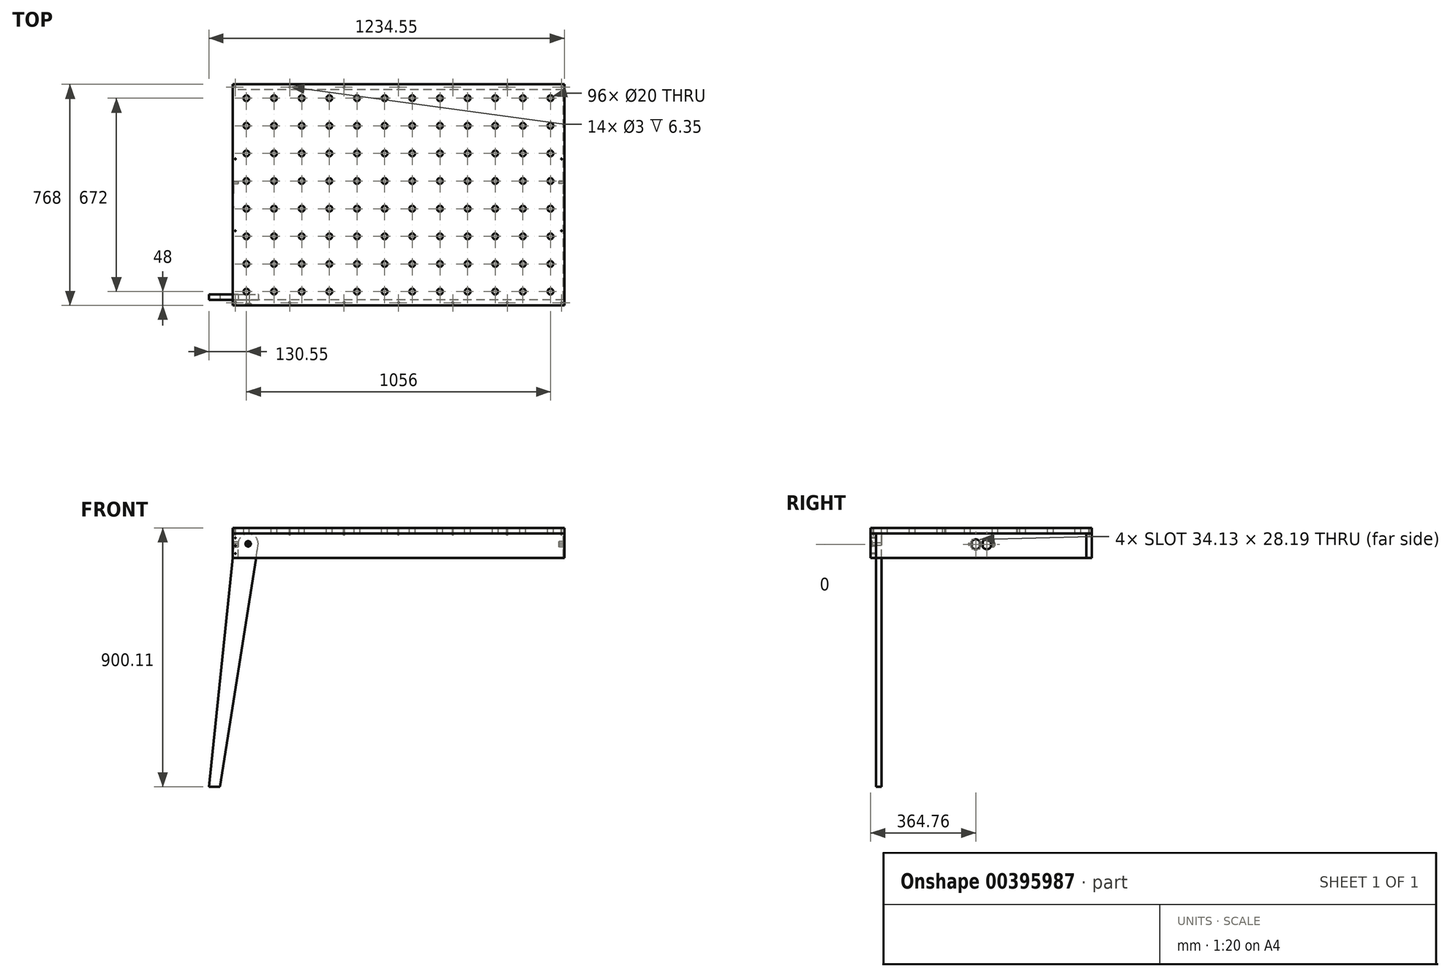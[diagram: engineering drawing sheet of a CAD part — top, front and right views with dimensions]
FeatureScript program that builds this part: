
annotation { "Feature Type Name" : "Feature", "Feature Type Description" : "" }
export const myFeature = defineFeature(function(context is Context, id is Id, definition is map)
    precondition{}
    {
        {
            var Q0;
            Q0=qCreatedBy(makeId("Top.planeOp"),FACE);
            var sketch = newSketch(context, id + "F0", { "sketchPlane" : qUnion([Q0])});
            skLineSegment(sketch, "E0.bottom", {"start": v(0, 0) * mm, "end": v(1152, 0) * mm});
            skLineSegment(sketch, "E0.top", {"start": v(0, 768) * mm, "end": v(1152, 768) * mm});
            skLineSegment(sketch, "E0.left", {"start": v(0, 0) * mm, "end": v(0, 768) * mm});
            skLineSegment(sketch, "E0.right", {"start": v(1152, 0) * mm, "end": v(1152, 768) * mm});
            skSolve(sketch);
        }
        {
            var Q0;
            Q0=makeQuery(id+"F0.imprint","IMPRINT",FACE,{"disambiguationData":[TD([[makeQuery(id+"F0.imprint","IMPRINT",EDGE,{"derivedFrom":sQuery(id+"F0.wireOp",EDGE,"E0.bottom")}),1.0]])]});
            extrude(context, id + "F1", {"entities" : qUnion([Q0]), "depth" : 19.05 * mm});
        }
        {
            var Q0;
            Q0=makeQuery(id+"F1.opExtrude","CAP_FACE",FACE,{"disambiguationData":[OSD([sQuery(id+"F0.wireOp",EDGE,"E0.bottom"),sQuery(id+"F0.wireOp",EDGE,"E0.top"),sQuery(id+"F0.wireOp",EDGE,"E0.left"),sQuery(id+"F0.wireOp",EDGE,"E0.right")])],"isStart":false});
            var sketch = newSketch(context, id + "F2", { "sketchPlane" : qUnion([Q0])});
            skLineSegment(sketch, "E1.0", {"start": v(1104, 720) * mm, "end": v(48, 720) * mm, "construction": true});
            skLineSegment(sketch, "E1.1", {"start": v(1104, 48) * mm, "end": v(1104, 720) * mm, "construction": true});
            skLineSegment(sketch, "E1.2", {"start": v(48, 48) * mm, "end": v(1104, 48) * mm, "construction": true});
            skLineSegment(sketch, "E1.3", {"start": v(48, 720) * mm, "end": v(48, 48) * mm, "construction": true});
            skCircle(sketch, "E2", {"center": v(48, 48) * mm, "radius": 10 * mm});
            skCircle(sketch, "E3.0.1.0", {"center": v(48, 144) * mm, "radius": 10 * mm});
            skCircle(sketch, "E3.0.2.0", {"center": v(48, 240) * mm, "radius": 10 * mm});
            skCircle(sketch, "E3.0.3.0", {"center": v(48, 336) * mm, "radius": 10 * mm});
            skCircle(sketch, "E3.0.4.0", {"center": v(48, 432) * mm, "radius": 10 * mm});
            skCircle(sketch, "E3.0.5.0", {"center": v(48, 528) * mm, "radius": 10 * mm});
            skCircle(sketch, "E3.0.6.0", {"center": v(48, 624) * mm, "radius": 10 * mm});
            skCircle(sketch, "E3.0.7.0", {"center": v(48, 720) * mm, "radius": 10 * mm});
            skCircle(sketch, "E3.1.0.0", {"center": v(144, 48) * mm, "radius": 10 * mm});
            skCircle(sketch, "E3.1.1.0", {"center": v(144, 144) * mm, "radius": 10 * mm});
            skCircle(sketch, "E3.1.2.0", {"center": v(144, 240) * mm, "radius": 10 * mm});
            skCircle(sketch, "E3.1.3.0", {"center": v(144, 336) * mm, "radius": 10 * mm});
            skCircle(sketch, "E3.1.4.0", {"center": v(144, 432) * mm, "radius": 10 * mm});
            skCircle(sketch, "E3.1.5.0", {"center": v(144, 528) * mm, "radius": 10 * mm});
            skCircle(sketch, "E3.1.6.0", {"center": v(144, 624) * mm, "radius": 10 * mm});
            skCircle(sketch, "E3.1.7.0", {"center": v(144, 720) * mm, "radius": 10 * mm});
            skCircle(sketch, "E3.2.0.0", {"center": v(240, 48) * mm, "radius": 10 * mm});
            skCircle(sketch, "E3.2.1.0", {"center": v(240, 144) * mm, "radius": 10 * mm});
            skCircle(sketch, "E3.2.2.0", {"center": v(240, 240) * mm, "radius": 10 * mm});
            skCircle(sketch, "E3.2.3.0", {"center": v(240, 336) * mm, "radius": 10 * mm});
            skCircle(sketch, "E3.2.4.0", {"center": v(240, 432) * mm, "radius": 10 * mm});
            skCircle(sketch, "E3.2.5.0", {"center": v(240, 528) * mm, "radius": 10 * mm});
            skCircle(sketch, "E3.2.6.0", {"center": v(240, 624) * mm, "radius": 10 * mm});
            skCircle(sketch, "E3.2.7.0", {"center": v(240, 720) * mm, "radius": 10 * mm});
            skCircle(sketch, "E3.3.0.0", {"center": v(336, 48) * mm, "radius": 10 * mm});
            skCircle(sketch, "E3.3.1.0", {"center": v(336, 144) * mm, "radius": 10 * mm});
            skCircle(sketch, "E3.3.2.0", {"center": v(336, 240) * mm, "radius": 10 * mm});
            skCircle(sketch, "E3.3.3.0", {"center": v(336, 336) * mm, "radius": 10 * mm});
            skCircle(sketch, "E3.3.4.0", {"center": v(336, 432) * mm, "radius": 10 * mm});
            skCircle(sketch, "E3.3.5.0", {"center": v(336, 528) * mm, "radius": 10 * mm});
            skCircle(sketch, "E3.3.6.0", {"center": v(336, 624) * mm, "radius": 10 * mm});
            skCircle(sketch, "E3.3.7.0", {"center": v(336, 720) * mm, "radius": 10 * mm});
            skCircle(sketch, "E3.4.0.0", {"center": v(432, 48) * mm, "radius": 10 * mm});
            skCircle(sketch, "E3.4.1.0", {"center": v(432, 144) * mm, "radius": 10 * mm});
            skCircle(sketch, "E3.4.2.0", {"center": v(432, 240) * mm, "radius": 10 * mm});
            skCircle(sketch, "E3.4.3.0", {"center": v(432, 336) * mm, "radius": 10 * mm});
            skCircle(sketch, "E3.4.4.0", {"center": v(432, 432) * mm, "radius": 10 * mm});
            skCircle(sketch, "E3.4.5.0", {"center": v(432, 528) * mm, "radius": 10 * mm});
            skCircle(sketch, "E3.4.6.0", {"center": v(432, 624) * mm, "radius": 10 * mm});
            skCircle(sketch, "E3.4.7.0", {"center": v(432, 720) * mm, "radius": 10 * mm});
            skCircle(sketch, "E3.5.0.0", {"center": v(528, 48) * mm, "radius": 10 * mm});
            skCircle(sketch, "E3.5.1.0", {"center": v(528, 144) * mm, "radius": 10 * mm});
            skCircle(sketch, "E3.5.2.0", {"center": v(528, 240) * mm, "radius": 10 * mm});
            skCircle(sketch, "E3.5.3.0", {"center": v(528, 336) * mm, "radius": 10 * mm});
            skCircle(sketch, "E3.5.4.0", {"center": v(528, 432) * mm, "radius": 10 * mm});
            skCircle(sketch, "E3.5.5.0", {"center": v(528, 528) * mm, "radius": 10 * mm});
            skCircle(sketch, "E3.5.6.0", {"center": v(528, 624) * mm, "radius": 10 * mm});
            skCircle(sketch, "E3.5.7.0", {"center": v(528, 720) * mm, "radius": 10 * mm});
            skCircle(sketch, "E3.6.0.0", {"center": v(624, 48) * mm, "radius": 10 * mm});
            skCircle(sketch, "E3.6.1.0", {"center": v(624, 144) * mm, "radius": 10 * mm});
            skCircle(sketch, "E3.6.2.0", {"center": v(624, 240) * mm, "radius": 10 * mm});
            skCircle(sketch, "E3.6.3.0", {"center": v(624, 336) * mm, "radius": 10 * mm});
            skCircle(sketch, "E3.6.4.0", {"center": v(624, 432) * mm, "radius": 10 * mm});
            skCircle(sketch, "E3.6.5.0", {"center": v(624, 528) * mm, "radius": 10 * mm});
            skCircle(sketch, "E3.6.6.0", {"center": v(624, 624) * mm, "radius": 10 * mm});
            skCircle(sketch, "E3.6.7.0", {"center": v(624, 720) * mm, "radius": 10 * mm});
            skCircle(sketch, "E3.7.0.0", {"center": v(720, 48) * mm, "radius": 10 * mm});
            skCircle(sketch, "E3.7.1.0", {"center": v(720, 144) * mm, "radius": 10 * mm});
            skCircle(sketch, "E3.7.2.0", {"center": v(720, 240) * mm, "radius": 10 * mm});
            skCircle(sketch, "E3.7.3.0", {"center": v(720, 336) * mm, "radius": 10 * mm});
            skCircle(sketch, "E3.7.4.0", {"center": v(720, 432) * mm, "radius": 10 * mm});
            skCircle(sketch, "E3.7.5.0", {"center": v(720, 528) * mm, "radius": 10 * mm});
            skCircle(sketch, "E3.7.6.0", {"center": v(720, 624) * mm, "radius": 10 * mm});
            skCircle(sketch, "E3.7.7.0", {"center": v(720, 720) * mm, "radius": 10 * mm});
            skCircle(sketch, "E3.8.0.0", {"center": v(816, 48) * mm, "radius": 10 * mm});
            skCircle(sketch, "E3.8.1.0", {"center": v(816, 144) * mm, "radius": 10 * mm});
            skCircle(sketch, "E3.8.2.0", {"center": v(816, 240) * mm, "radius": 10 * mm});
            skCircle(sketch, "E3.8.3.0", {"center": v(816, 336) * mm, "radius": 10 * mm});
            skCircle(sketch, "E3.8.4.0", {"center": v(816, 432) * mm, "radius": 10 * mm});
            skCircle(sketch, "E3.8.5.0", {"center": v(816, 528) * mm, "radius": 10 * mm});
            skCircle(sketch, "E3.8.6.0", {"center": v(816, 624) * mm, "radius": 10 * mm});
            skCircle(sketch, "E3.8.7.0", {"center": v(816, 720) * mm, "radius": 10 * mm});
            skCircle(sketch, "E3.9.0.0", {"center": v(912, 48) * mm, "radius": 10 * mm});
            skCircle(sketch, "E3.9.1.0", {"center": v(912, 144) * mm, "radius": 10 * mm});
            skCircle(sketch, "E3.9.2.0", {"center": v(912, 240) * mm, "radius": 10 * mm});
            skCircle(sketch, "E3.9.3.0", {"center": v(912, 336) * mm, "radius": 10 * mm});
            skCircle(sketch, "E3.9.4.0", {"center": v(912, 432) * mm, "radius": 10 * mm});
            skCircle(sketch, "E3.9.5.0", {"center": v(912, 528) * mm, "radius": 10 * mm});
            skCircle(sketch, "E3.9.6.0", {"center": v(912, 624) * mm, "radius": 10 * mm});
            skCircle(sketch, "E3.9.7.0", {"center": v(912, 720) * mm, "radius": 10 * mm});
            skCircle(sketch, "E3.10.0.0", {"center": v(1008, 48) * mm, "radius": 10 * mm});
            skCircle(sketch, "E3.10.1.0", {"center": v(1008, 144) * mm, "radius": 10 * mm});
            skCircle(sketch, "E3.10.2.0", {"center": v(1008, 240) * mm, "radius": 10 * mm});
            skCircle(sketch, "E3.10.3.0", {"center": v(1008, 336) * mm, "radius": 10 * mm});
            skCircle(sketch, "E3.10.4.0", {"center": v(1008, 432) * mm, "radius": 10 * mm});
            skCircle(sketch, "E3.10.5.0", {"center": v(1008, 528) * mm, "radius": 10 * mm});
            skCircle(sketch, "E3.10.6.0", {"center": v(1008, 624) * mm, "radius": 10 * mm});
            skCircle(sketch, "E3.10.7.0", {"center": v(1008, 720) * mm, "radius": 10 * mm});
            skCircle(sketch, "E3.11.0.0", {"center": v(1104, 48) * mm, "radius": 10 * mm});
            skCircle(sketch, "E3.11.1.0", {"center": v(1104, 144) * mm, "radius": 10 * mm});
            skCircle(sketch, "E3.11.2.0", {"center": v(1104, 240) * mm, "radius": 10 * mm});
            skCircle(sketch, "E3.11.3.0", {"center": v(1104, 336) * mm, "radius": 10 * mm});
            skCircle(sketch, "E3.11.4.0", {"center": v(1104, 432) * mm, "radius": 10 * mm});
            skCircle(sketch, "E3.11.5.0", {"center": v(1104, 528) * mm, "radius": 10 * mm});
            skCircle(sketch, "E3.11.6.0", {"center": v(1104, 624) * mm, "radius": 10 * mm});
            skCircle(sketch, "E3.11.7.0", {"center": v(1104, 720) * mm, "radius": 10 * mm});
            skLineSegment(sketch, "E3.direction1", {"start": v(48, 48) * mm, "end": v(144, 48) * mm, "construction": true});
            skLineSegment(sketch, "E3.direction2", {"start": v(48, 48) * mm, "end": v(48, 144) * mm, "construction": true});
            skSolve(sketch);
        }
        {
            var Q0;
            Q0=qSketchRegion(id+"F2",true);
            extrude(context, id + "F3", {"entities" : qUnion([Q0]), "operationType" : NewBodyOperationType.REMOVE, "endBound" : BoundingType.THROUGH_ALL, "oppositeDirection" : true, "depth" : 25.4 * mm});
        }
        {
            var Q0;
            Q0=qCreatedBy(makeId("Right.planeOp"),FACE);
            var sketch = newSketch(context, id + "F4", { "sketchPlane" : qUnion([Q0])});
            skLineSegment(sketch, "E4.bottom", {"start": v(0, 0) * mm, "end": v(19.05, 0) * mm});
            skLineSegment(sketch, "E4.top", {"start": v(0, -85.95) * mm, "end": v(19.05, -85.95) * mm});
            skLineSegment(sketch, "E4.left", {"start": v(0, 0) * mm, "end": v(0, -85.95) * mm});
            skLineSegment(sketch, "E4.right", {"start": v(19.05, 0) * mm, "end": v(19.05, -85.95) * mm});
            skSolve(sketch);
        }
        {
            var Q0;
            Q0=qSketchRegion(id+"F4",true);
            var Q1;
            Q1=makeQuery(id+"F1.opExtrude","SWEPT_FACE",FACE,{"disambiguationData":[OSD([sQuery(id+"F0.wireOp",EDGE,"E0.right")])]});
            extrude(context, id + "F5", {"entities" : qUnion([Q0]), "endBound" : BoundingType.UP_TO_SURFACE, "endBoundEntityFace" : qUnion([Q1]), "depth" : 25.4 * mm});
        }
        {
            var Q0;
            Q0=makeQuery(id+"F5.opExtrude","SWEPT_FACE",FACE,{"disambiguationData":[OSD([sQuery(id+"F4.wireOp",EDGE,"E4.right")])]});
            var sketch = newSketch(context, id + "F6", { "sketchPlane" : qUnion([Q0])});
            skLineSegment(sketch, "E5.bottom", {"start": v(0, 0) * mm, "end": v(-19.05, 0) * mm});
            skLineSegment(sketch, "E5.top", {"start": v(0, -85.95) * mm, "end": v(-19.05, -85.95) * mm});
            skLineSegment(sketch, "E5.left", {"start": v(0, 0) * mm, "end": v(0, -85.95) * mm});
            skLineSegment(sketch, "E5.right", {"start": v(-19.05, 0) * mm, "end": v(-19.05, -85.95) * mm});
            skSolve(sketch);
        }
        {
            var Q0;
            Q0=makeQuery(id+"F1.opExtrude","CAP_FACE",FACE,{"disambiguationData":[OSD([sQuery(id+"F0.wireOp",EDGE,"E0.bottom"),sQuery(id+"F0.wireOp",EDGE,"E0.top"),sQuery(id+"F0.wireOp",EDGE,"E0.left"),sQuery(id+"F0.wireOp",EDGE,"E0.right")])],"isStart":false});
            var sketch = newSketch(context, id + "F7", { "sketchPlane" : qUnion([Q0])});
            skCircle(sketch, "E6", {"center": v(9.52, 9.53) * mm, "radius": 1.5 * mm});
            skCircle(sketch, "E7", {"center": v(198.35, 9.53) * mm, "radius": 1.5 * mm});
            skCircle(sketch, "E8", {"center": v(387.18, 9.53) * mm, "radius": 1.5 * mm});
            skCircle(sketch, "E9", {"center": v(576, 9.53) * mm, "radius": 1.5 * mm});
            skCircle(sketch, "E10", {"center": v(764.83, 9.53) * mm, "radius": 1.5 * mm});
            skCircle(sketch, "E11", {"center": v(953.65, 9.53) * mm, "radius": 1.5 * mm});
            skCircle(sketch, "E12", {"center": v(1142.48, 9.53) * mm, "radius": 1.5 * mm});
            skLineSegment(sketch, "E13", {"start": v(9.53, 9.53) * mm, "end": v(198.35, 9.53) * mm, "construction": true});
            skLineSegment(sketch, "E14", {"start": v(387.18, 9.53) * mm, "end": v(198.35, 9.53) * mm, "construction": true});
            skLineSegment(sketch, "E15", {"start": v(387.18, 9.53) * mm, "end": v(576, 9.53) * mm, "construction": true});
            skLineSegment(sketch, "E16", {"start": v(576, 9.53) * mm, "end": v(764.83, 9.53) * mm, "construction": true});
            skLineSegment(sketch, "E17", {"start": v(764.83, 9.53) * mm, "end": v(953.65, 9.53) * mm, "construction": true});
            skLineSegment(sketch, "E18", {"start": v(953.65, 9.53) * mm, "end": v(1142.48, 9.53) * mm, "construction": true});
            skLineSegment(sketch, "E19", {"start": v(1142.48, 9.53) * mm, "end": v(1152, 9.53) * mm, "construction": true});
            skLineSegment(sketch, "E20", {"start": v(1142.48, 9.53) * mm, "end": v(1142.48, 0) * mm, "construction": true});
            skLineSegment(sketch, "E21", {"start": v(9.52, 9.53) * mm, "end": v(0, 9.53) * mm, "construction": true});
            skCircle(sketch, "E22", {"center": v(9.52, 259.18) * mm, "radius": 1.5 * mm});
            skCircle(sketch, "E23", {"center": v(9.52, 508.83) * mm, "radius": 1.5 * mm});
            skCircle(sketch, "E24", {"center": v(9.52, 758.48) * mm, "radius": 1.5 * mm});
            skLineSegment(sketch, "E25", {"start": v(9.52, 758.48) * mm, "end": v(9.52, 768) * mm, "construction": true});
            skLineSegment(sketch, "E26", {"start": v(9.52, 9.53) * mm, "end": v(9.53, 0) * mm, "construction": true});
            skLineSegment(sketch, "E27", {"start": v(9.52, 9.53) * mm, "end": v(9.52, 259.18) * mm, "construction": true});
            skLineSegment(sketch, "E28", {"start": v(9.52, 259.18) * mm, "end": v(9.52, 508.83) * mm, "construction": true});
            skLineSegment(sketch, "E29", {"start": v(9.52, 508.83) * mm, "end": v(9.52, 758.48) * mm, "construction": true});
            skLineSegment(sketch, "E30", {"start": v(0, 384) * mm, "end": v(1152, 384) * mm, "construction": true});
            skLineSegment(sketch, "E31", {"start": v(576, 768) * mm, "end": v(576, 0) * mm, "construction": true});
            skCircle(sketch, "E32.MirrorC", {"center": v(1142.48, 758.48) * mm, "radius": 1.5 * mm});
            skCircle(sketch, "E33.MirrorC", {"center": v(1142.48, 259.18) * mm, "radius": 1.5 * mm});
            skCircle(sketch, "E34.MirrorC", {"center": v(1142.48, 508.83) * mm, "radius": 1.5 * mm});
            skCircle(sketch, "E35.MirrorC", {"center": v(198.35, 758.48) * mm, "radius": 1.5 * mm});
            skCircle(sketch, "E36.MirrorC", {"center": v(387.18, 758.48) * mm, "radius": 1.5 * mm});
            skCircle(sketch, "E37.MirrorC", {"center": v(576, 758.48) * mm, "radius": 1.5 * mm});
            skCircle(sketch, "E38.MirrorC", {"center": v(764.83, 758.47) * mm, "radius": 1.5 * mm});
            skCircle(sketch, "E39.MirrorC", {"center": v(953.65, 758.47) * mm, "radius": 1.5 * mm});
            skSolve(sketch);
        }
        {
            var Q0;
            Q0=sQuery(id+"F7.wireOp",EDGE,"E30");
            cPlane(context, id + "F8", {"entities" : qUnion([Q0]), "cplaneType" : CPlaneType.LINE_ANGLE, "offset" : 25.4 * mm, "angle" : 0 * degree, "width" : 152.4 * mm, "height" : 152.4 * mm});
        }
        {
            var Q0;
            Q0=makeQuery(id+"F5.opExtrude","SWEPT_BODY",BODY,{"disambiguationData":[OSD([sQuery(id+"F4.wireOp",EDGE,"E4.bottom"),sQuery(id+"F4.wireOp",EDGE,"E4.top"),sQuery(id+"F4.wireOp",EDGE,"E4.left"),sQuery(id+"F4.wireOp",EDGE,"E4.right")])]});
            var Q1;
            Q1=qCreatedBy(id+"F8.planeOp",FACE);
            mirror(context, id + "F9", {"entities" : qUnion([Q0]), "mirrorPlane" : qUnion([Q1])});
        }
        {
            var Q0;
            Q0=makeQuery(id+"F6.imprint","IMPRINT",FACE,{"disambiguationData":[TD([[makeQuery(id+"F6.imprint","IMPRINT",EDGE,{"derivedFrom":sQuery(id+"F6.wireOp",EDGE,"E5.bottom")}),-1.0]])]});
            var Q1;
            Q1=makeQuery(id+"F9.opPattern","COPY",FACE,{"derivedFrom":makeQuery(id+"F5.opExtrude","SWEPT_FACE",FACE,{"disambiguationData":[OSD([sQuery(id+"F4.wireOp",EDGE,"E4.right")])]}),"instanceName":"1"});
            extrude(context, id + "F10", {"entities" : qUnion([Q0]), "endBound" : BoundingType.UP_TO_SURFACE, "endBoundEntityFace" : qUnion([Q1]), "depth" : 25.4 * mm});
        }
        {
            var Q0;
            Q0=qSketchRegion(id+"F7",true);
            extrude(context, id + "F11", {"entities" : qUnion([Q0]), "operationType" : NewBodyOperationType.REMOVE, "oppositeDirection" : true, "depth" : 25.4 * mm});
        }
        {
            var Q0;
            Q0=makeQuery(id+"F5.opExtrude","SWEPT_FACE",FACE,{"disambiguationData":[OSD([sQuery(id+"F4.wireOp",EDGE,"E4.right")])]});
            var sketch = newSketch(context, id + "F12", { "sketchPlane" : qUnion([Q0])});
            skLineSegment(sketch, "E40", {"start": v(-19.05, -36.51) * mm, "end": v(-19.05, -881.06) * mm, "construction": true});
            skLineSegment(sketch, "E41", {"start": v(44.45, -881.06) * mm, "end": v(-88.47, -41.98) * mm});
            skArc(sketch, "E42", {"start": v(-19.05, -36.51) * mm, "mid": v(-56.72, -1.7) * mm, "end": v(-88.47, -41.98) * mm});
            skLineSegment(sketch, "E43", {"start": v(-19.05, -85.95) * mm, "end": v(0, -85.95) * mm});
            skLineSegment(sketch, "E44", {"start": v(0, -85.95) * mm, "end": v(82.55, -881.06) * mm});
            skLineSegment(sketch, "E45", {"start": v(82.55, -881.06) * mm, "end": v(44.45, -881.06) * mm});
            skLineSegment(sketch, "E46", {"start": v(-19.05, -881.06) * mm, "end": v(-19.05, 19.05) * mm, "construction": true});
            skLineSegment(sketch, "E47", {"start": v(-19.05, -85.95) * mm, "end": v(-19.05, -36.51) * mm});
            skSolve(sketch);
        }
        {
            var Q0;
            Q0=qSketchRegion(id+"F12",true);
            extrude(context, id + "F13", {"entities" : qUnion([Q0]), "depth" : 19.05 * mm});
        }
        {
            var Q0;
            Q0=makeQuery(id+"F13.opExtrude","CAP_FACE",FACE,{"disambiguationData":[OSD([sQuery(id+"F12.wireOp",EDGE,"E41"),sQuery(id+"F12.wireOp",EDGE,"E42"),sQuery(id+"F12.wireOp",EDGE,"E43"),sQuery(id+"F12.wireOp",EDGE,"E44"),sQuery(id+"F12.wireOp",EDGE,"E45"),sQuery(id+"F12.wireOp",EDGE,"E47")])],"isStart":false});
            var sketch = newSketch(context, id + "F14", { "sketchPlane" : qUnion([Q0])});
            skCircle(sketch, "E48", {"center": v(-53.97, -36.51) * mm, "radius": 4.76 * mm});
            skSolve(sketch);
        }
        {
            var Q0;
            Q0=qSketchRegion(id+"F14",true);
            extrude(context, id + "F15", {"entities" : qUnion([Q0]), "operationType" : NewBodyOperationType.REMOVE, "endBound" : BoundingType.THROUGH_ALL, "oppositeDirection" : true, "depth" : 25.4 * mm});
        }
        {
            var Q0;
            Q0=makeQuery(id+"F5.opExtrude","SWEPT_FACE",FACE,{"disambiguationData":[OSD([sQuery(id+"F4.wireOp",EDGE,"E4.left")])]});
            var sketch = newSketch(context, id + "F16", { "sketchPlane" : qUnion([Q0])});
            skCircle(sketch, "E49", {"center": v(53.97, -36.51) * mm, "radius": 9.53 * mm});
            skSolve(sketch);
        }
        {
            var Q0;
            Q0=qSketchRegion(id+"F16",true);
            extrude(context, id + "F17", {"entities" : qUnion([Q0]), "operationType" : NewBodyOperationType.REMOVE, "oppositeDirection" : true, "depth" : 6.35 * mm});
        }
        {
            var Q0;
            Q0=makeQuery(id+"F5.opExtrude","SWEPT_FACE",FACE,{"disambiguationData":[OSD([sQuery(id+"F4.wireOp",EDGE,"E4.left")])]});
            var sketch = newSketch(context, id + "F18", { "sketchPlane" : qUnion([Q0])});
            skCircle(sketch, "E50", {"center": v(9.52, -15.88) * mm, "radius": 1.5 * mm});
            skCircle(sketch, "E51", {"center": v(9.53, -42.98) * mm, "radius": 1.5 * mm});
            skCircle(sketch, "E52", {"center": v(9.53, -70.08) * mm, "radius": 1.5 * mm});
            skLineSegment(sketch, "E53", {"start": v(9.52, 0) * mm, "end": v(9.52, -15.88) * mm, "construction": true});
            skLineSegment(sketch, "E54", {"start": v(9.53, -85.95) * mm, "end": v(9.53, -70.08) * mm, "construction": true});
            skLineSegment(sketch, "E55", {"start": v(9.52, -15.88) * mm, "end": v(9.53, -70.08) * mm, "construction": true});
            skSolve(sketch);
        }
        {
            var Q0;
            Q0=qSketchRegion(id+"F18",true);
            extrude(context, id + "F19", {"entities" : qUnion([Q0]), "operationType" : NewBodyOperationType.REMOVE, "oppositeDirection" : true, "depth" : 41.27 * mm});
        }
        {
            var Q0;
            Q0=makeQuery(id+"F10.opExtrude","SWEPT_FACE",FACE,{"disambiguationData":[OSD([sQuery(id+"F6.wireOp",EDGE,"E5.right")])]});
            var sketch = newSketch(context, id + "F20", { "sketchPlane" : qUnion([Q0])});
            skLineSegment(sketch, "E56.bottom", {"start": v(422.9, -12.7) * mm, "end": v(345.1, -12.7) * mm});
            skLineSegment(sketch, "E56.top", {"start": v(422.9, -63.5) * mm, "end": v(345.1, -63.5) * mm});
            skLineSegment(sketch, "E56.left", {"start": v(422.9, -12.7) * mm, "end": v(422.9, -63.5) * mm});
            skLineSegment(sketch, "E56.right", {"start": v(345.1, -12.7) * mm, "end": v(345.1, -63.5) * mm});
            skPoint(sketch, "E56.middle", {"position": v(384, -38.1) * mm});
            skPoint(sketch, "E56.middle.positionSnap0", {"position": v(384, 0) * mm});
            skPoint(sketch, "E56.centerSnap0", {"position": v(384, 0) * mm});
            skSolve(sketch);
        }
        {
            var Q0;
            Q0=makeQuery(id+"F20.imprint","IMPRINT",FACE,{"disambiguationData":[TD([[makeQuery(id+"F20.imprint","IMPRINT",EDGE,{"derivedFrom":sQuery(id+"F20.wireOp",EDGE,"E56.bottom")}),1.0]])]});
            extrude(context, id + "F21", {"entities" : qUnion([Q0]), "operationType" : NewBodyOperationType.REMOVE, "oppositeDirection" : true, "depth" : 15.88 * mm});
        }
        {
            var Q0;
            Q0=makeQuery(id+"F21.boolean.opBoolean","COPY",FACE,{"derivedFrom":makeQuery(id+"F21.opExtrude","CAP_FACE",FACE,{"disambiguationData":[OSD([sQuery(id+"F20.wireOp",EDGE,"E56.bottom"),sQuery(id+"F20.wireOp",EDGE,"E56.top"),sQuery(id+"F20.wireOp",EDGE,"E56.left"),sQuery(id+"F20.wireOp",EDGE,"E56.right")])],"isStart":false})});
            var sketch = newSketch(context, id + "F22", { "sketchPlane" : qUnion([Q0])});
            skArc(sketch, "E57", {"start": v(389.14, -47.72) * mm, "mid": v(403.24, -55.17) * mm, "end": v(417.34, -47.72) * mm});
            skArc(sketch, "E58", {"start": v(350.66, -47.72) * mm, "mid": v(364.76, -55.17) * mm, "end": v(378.86, -47.72) * mm});
            skLineSegment(sketch, "E59", {"start": v(350.66, -47.72) * mm, "end": v(350.66, -28.48) * mm});
            skLineSegment(sketch, "E60", {"start": v(378.86, -28.48) * mm, "end": v(378.86, -47.72) * mm});
            skLineSegment(sketch, "E61", {"start": v(389.14, -28.48) * mm, "end": v(389.14, -47.72) * mm});
            skLineSegment(sketch, "E62", {"start": v(417.34, -28.48) * mm, "end": v(417.34, -47.72) * mm});
            skLineSegment(sketch, "E63", {"start": v(350.66, -28.48) * mm, "end": v(378.86, -28.48) * mm, "construction": true});
            skLineSegment(sketch, "E64", {"start": v(389.14, -28.48) * mm, "end": v(417.34, -28.48) * mm, "construction": true});
            skLineSegment(sketch, "E65", {"start": v(345.1, -38.1) * mm, "end": v(422.9, -38.1) * mm, "construction": true});
            skLineSegment(sketch, "E66", {"start": v(364.76, -38.1) * mm, "end": v(403.24, -38.1) * mm, "construction": true});
            skLineSegment(sketch, "E67", {"start": v(384, -38.1) * mm, "end": v(384, -43.41) * mm, "construction": true});
            skArc(sketch, "E68.trimOffspring", {"start": v(378.86, -28.48) * mm, "mid": v(364.76, -21.03) * mm, "end": v(350.66, -28.48) * mm});
            skLineSegment(sketch, "E69.trimOffspring", {"start": v(381.83, -38.1) * mm, "end": v(381.83, -38.1) * mm});
            skLineSegment(sketch, "E70.trimOffspring", {"start": v(386.17, -38.1) * mm, "end": v(386.17, -38.1) * mm});
            skArc(sketch, "E71.trimOffspring", {"start": v(417.34, -28.48) * mm, "mid": v(403.24, -21.03) * mm, "end": v(389.14, -28.48) * mm});
            skSolve(sketch);
        }
        {
            var Q0;
            Q0=qSketchRegion(id+"F22",true);
            extrude(context, id + "F23", {"entities" : qUnion([Q0]), "operationType" : NewBodyOperationType.REMOVE, "endBound" : BoundingType.THROUGH_ALL, "oppositeDirection" : true, "depth" : 25.4 * mm});
        }
        {
            var Q0;
            Q0=makeQuery(id+"F10.opExtrude","SWEPT_FACE",FACE,{"disambiguationData":[OSD([sQuery(id+"F6.wireOp",EDGE,"E5.right")])]});
            var sketch = newSketch(context, id + "F24", { "sketchPlane" : qUnion([Q0])});
            skArc(sketch, "E72", {"start": v(345.1, -28.57) * mm, "mid": v(335.58, -38.1) * mm, "end": v(345.1, -47.62) * mm});
            skArc(sketch, "E73.MirrorCS", {"start": v(345.1, 3.18) * mm, "mid": v(335.58, 12.7) * mm, "end": v(345.1, 22.23) * mm});
            skLineSegment(sketch, "E74", {"start": v(384, -12.7) * mm, "end": v(384, -63.5) * mm, "construction": true});
            skArc(sketch, "E75.MirrorCS", {"start": v(422.9, -28.57) * mm, "mid": v(432.42, -38.1) * mm, "end": v(422.9, -47.62) * mm});
            skSolve(sketch);
        }
        {
            var Q0;
            {var subQ0=sQuery(id+"F24.wireOp",EDGE,"E72");Q0=makeQuery(id+"F24.imprint","IMPRINT",FACE,{"disambiguationData":[TD([[makeQuery(id+"F24.imprint","IMPRINT",EDGE,{"derivedFrom":subQ0}),1.0]])]});}
            var Q1;
            {var subQ0=sQuery(id+"F24.wireOp",EDGE,"E75.MirrorCS");Q1=makeQuery(id+"F24.imprint","IMPRINT",FACE,{"disambiguationData":[TD([[makeQuery(id+"F24.imprint","IMPRINT",EDGE,{"derivedFrom":subQ0}),-1.0]])]});}
            var Q2;
            Q2=makeQuery(id+"F21.boolean.opBoolean","COPY",FACE,{"derivedFrom":makeQuery(id+"F21.opExtrude","CAP_FACE",FACE,{"disambiguationData":[OSD([sQuery(id+"F20.wireOp",EDGE,"E56.bottom"),sQuery(id+"F20.wireOp",EDGE,"E56.top"),sQuery(id+"F20.wireOp",EDGE,"E56.left"),sQuery(id+"F20.wireOp",EDGE,"E56.right")])],"isStart":false})});
            extrude(context, id + "F25", {"entities" : qUnion([Q0, Q1]), "operationType" : NewBodyOperationType.REMOVE, "endBound" : BoundingType.UP_TO_SURFACE, "oppositeDirection" : true, "endBoundEntityFace" : qUnion([Q2]), "depth" : 15.88 * mm});
        }
        {
            var Q0;
            {var subQ6=sQuery(id+"F24.wireOp",EDGE,"E72");Q0=makeQuery(id+"F24.imprint","IMPRINT",FACE,{"disambiguationData":[TD([[makeQuery(id+"F24.imprint","IMPRINT",EDGE,{"derivedFrom":subQ6}),-1.0]])]});}
            var sketch = newSketch(context, id + "F26", { "sketchPlane" : qUnion([Q0])});
            skLineSegment(sketch, "E76", {"start": v(384, -38.1) * mm, "end": v(341.53, -38.1) * mm, "construction": true});
            skCircle(sketch, "E77", {"center": v(341.53, -38.1) * mm, "radius": 3.18 * mm});
            skCircle(sketch, "E78.MirrorC", {"center": v(426.47, -38.1) * mm, "radius": 3.18 * mm});
            skSolve(sketch);
        }
        {
            var Q0;
            Q0=qSketchRegion(id+"F26",true);
            extrude(context, id + "F27", {"entities" : qUnion([Q0]), "operationType" : NewBodyOperationType.REMOVE, "oppositeDirection" : true, "depth" : 17.46 * mm});
        }
        {
            var Q0;
            Q0=sQuery(id+"F7.wireOp",EDGE,"E31");
            cPlane(context, id + "F28", {"entities" : qUnion([Q0]), "cplaneType" : CPlaneType.LINE_ANGLE, "offset" : 25.4 * mm, "angle" : 90 * degree, "width" : 152.4 * mm, "height" : 152.4 * mm});
        }
        {
            var Q0;
            Q0=makeQuery(id+"F10.opExtrude","SWEPT_BODY",BODY,{"disambiguationData":[OSD([sQuery(id+"F6.wireOp",EDGE,"E5.bottom"),sQuery(id+"F6.wireOp",EDGE,"E5.top"),sQuery(id+"F6.wireOp",EDGE,"E5.left"),sQuery(id+"F6.wireOp",EDGE,"E5.right")])]});
            var Q1;
            Q1=qCreatedBy(id+"F28.planeOp",FACE);
            mirror(context, id + "F29", {"entities" : qUnion([Q0]), "mirrorPlane" : qUnion([Q1])});
        }
    });
